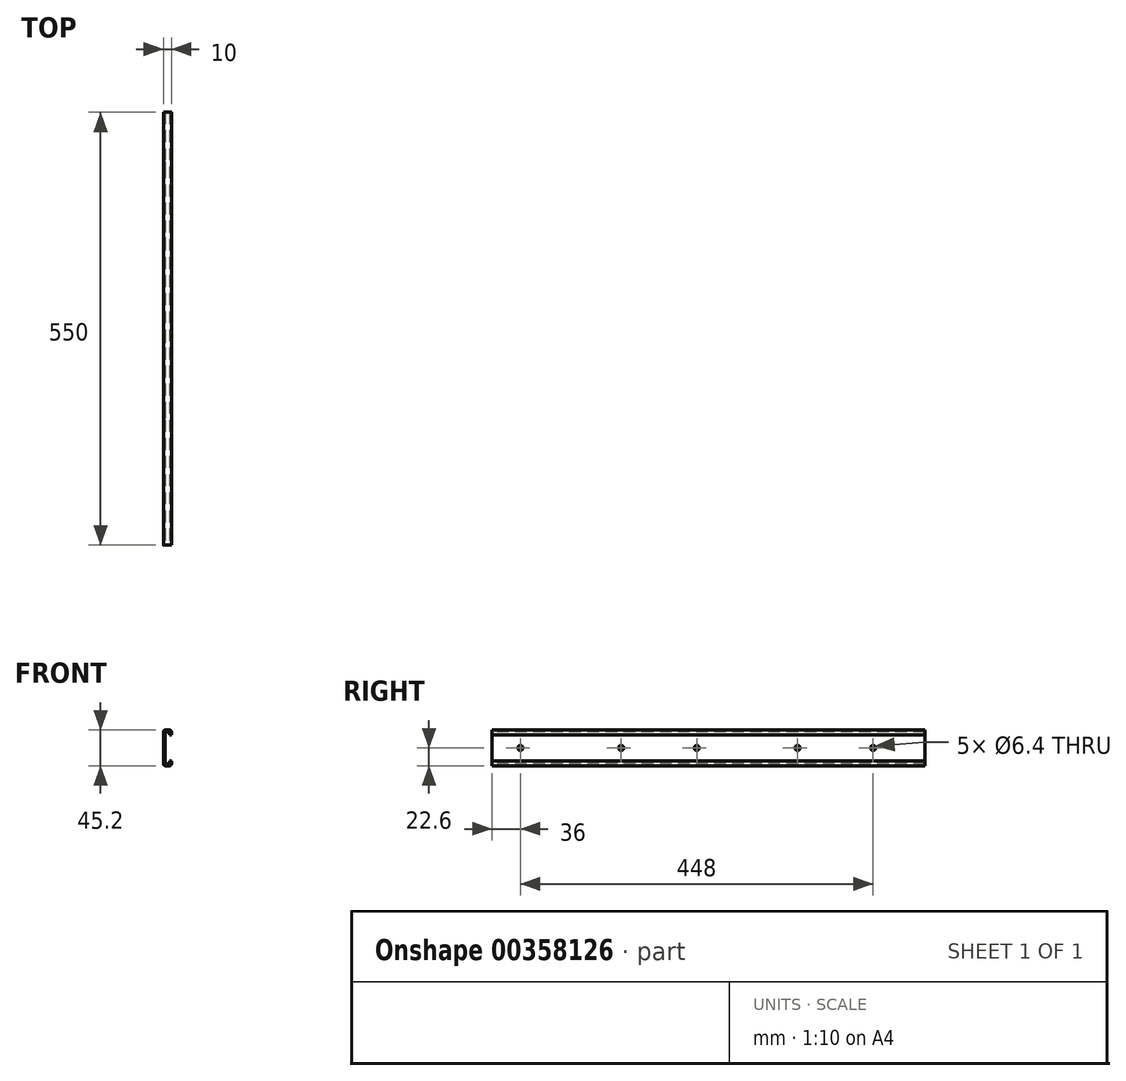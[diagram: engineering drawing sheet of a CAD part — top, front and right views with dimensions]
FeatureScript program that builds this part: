
annotation { "Feature Type Name" : "Feature", "Feature Type Description" : "" }
export const myFeature = defineFeature(function(context is Context, id is Id, definition is map)
    precondition{}
    {
        {
            var Q0;
            Q0=qCreatedBy(makeId("Front.planeOp"),FACE);
            var sketch = newSketch(context, id + "F0", { "sketchPlane" : qUnion([Q0])});
            skLineSegment(sketch, "E0.bottom", {"start": v(2, 0) * mm, "end": v(8, 0) * mm});
            skLineSegment(sketch, "E0.top", {"start": v(2, 45.2) * mm, "end": v(8, 45.2) * mm});
            skLineSegment(sketch, "E0.left", {"start": v(0, 2) * mm, "end": v(0, 43.2) * mm});
            skLineSegment(sketch, "E0.right", {"start": v(10, 2) * mm, "end": v(10, 6) * mm});
            skPoint(sketch, "E1.visualSharp", {"position": v(0, 45.2) * mm});
            skArc(sketch, "E1.filletArc", {"start": v(2, 45.2) * mm, "mid": v(0.59, 44.61) * mm, "end": v(0, 43.2) * mm});
            skPoint(sketch, "E2.visualSharp", {"position": v(10, 45.2) * mm});
            skArc(sketch, "E2.filletArc", {"start": v(10, 43.2) * mm, "mid": v(9.41, 44.61) * mm, "end": v(8, 45.2) * mm});
            skPoint(sketch, "E3.visualSharp", {"position": v(0, 0) * mm});
            skArc(sketch, "E3.filletArc", {"start": v(0, 2) * mm, "mid": v(0.59, 0.59) * mm, "end": v(2, 0) * mm});
            skPoint(sketch, "E4.visualSharp", {"position": v(10, 0) * mm});
            skArc(sketch, "E4.filletArc", {"start": v(8, 0) * mm, "mid": v(9.41, 0.59) * mm, "end": v(10, 2) * mm});
            skLineSegment(sketch, "E5.bottom", {"start": v(7, 2) * mm, "end": v(3, 2) * mm});
            skLineSegment(sketch, "E5.top", {"start": v(7, 43.2) * mm, "end": v(3, 43.2) * mm});
            skLineSegment(sketch, "E5.left", {"start": v(8, 3) * mm, "end": v(8, 6) * mm});
            skLineSegment(sketch, "E5.right", {"start": v(2, 3) * mm, "end": v(2, 42.2) * mm});
            skLineSegment(sketch, "E6", {"start": v(10, 43.2) * mm, "end": v(10, 39.2) * mm});
            skLineSegment(sketch, "E7", {"start": v(10, 39.2) * mm, "end": v(8, 39.2) * mm});
            skLineSegment(sketch, "E8", {"start": v(10, 6) * mm, "end": v(8, 6) * mm});
            skLineSegment(sketch, "E9.trimOffspring", {"start": v(10, 39.2) * mm, "end": v(10, 43.2) * mm});
            skLineSegment(sketch, "E10.trimOffspring", {"start": v(8, 39.2) * mm, "end": v(8, 42.2) * mm});
            skArc(sketch, "E11.filletArc", {"start": v(3, 43.2) * mm, "mid": v(2.3, 42.9) * mm, "end": v(2, 42.2) * mm});
            skArc(sketch, "E12.filletArc", {"start": v(8, 42.2) * mm, "mid": v(7.7, 42.9) * mm, "end": v(7, 43.2) * mm});
            skArc(sketch, "E13.filletArc", {"start": v(2, 3) * mm, "mid": v(2.3, 2.3) * mm, "end": v(3, 2) * mm});
            skArc(sketch, "E14.filletArc", {"start": v(7, 2) * mm, "mid": v(7.7, 2.3) * mm, "end": v(8, 3) * mm});
            skSolve(sketch);
        }
        {
            var Q0;
            Q0=makeQuery(id+"F0.imprint","IMPRINT",FACE,{"disambiguationData":[TD([[makeQuery(id+"F0.imprint","IMPRINT",EDGE,{"derivedFrom":sQuery(id+"F0.wireOp",EDGE,"E0.bottom")}),1.0]])]});
            extrude(context, id + "F1", {"entities" : qUnion([Q0]), "depth" : -550 * mm});
        }
        {
            var Q0;
            Q0=makeQuery(id+"F1.opExtrude","SWEPT_FACE",FACE,{"disambiguationData":[OSD([sQuery(id+"F0.wireOp",EDGE,"E0.left")])]});
            var sketch = newSketch(context, id + "F2", { "sketchPlane" : qUnion([Q0])});
            skLineSegment(sketch, "E15", {"start": v(0, 22.6) * mm, "end": v(-550, 22.6) * mm, "construction": true});
            skCircle(sketch, "E16", {"center": v(-36, 22.6) * mm, "radius": 3.2 * mm});
            skCircle(sketch, "E17", {"center": v(-164, 22.6) * mm, "radius": 3.2 * mm});
            skCircle(sketch, "E18", {"center": v(-260, 22.6) * mm, "radius": 3.2 * mm});
            skCircle(sketch, "E19", {"center": v(-388, 22.6) * mm, "radius": 3.2 * mm});
            skCircle(sketch, "E20", {"center": v(-484, 22.6) * mm, "radius": 3.2 * mm});
            skSolve(sketch);
        }
        {
            var Q0;
            Q0=qSketchRegion(id+"F2",true);
            extrude(context, id + "F3", {"entities" : qUnion([Q0]), "operationType" : NewBodyOperationType.REMOVE, "oppositeDirection" : true, "depth" : 2 * mm});
        }
    });
